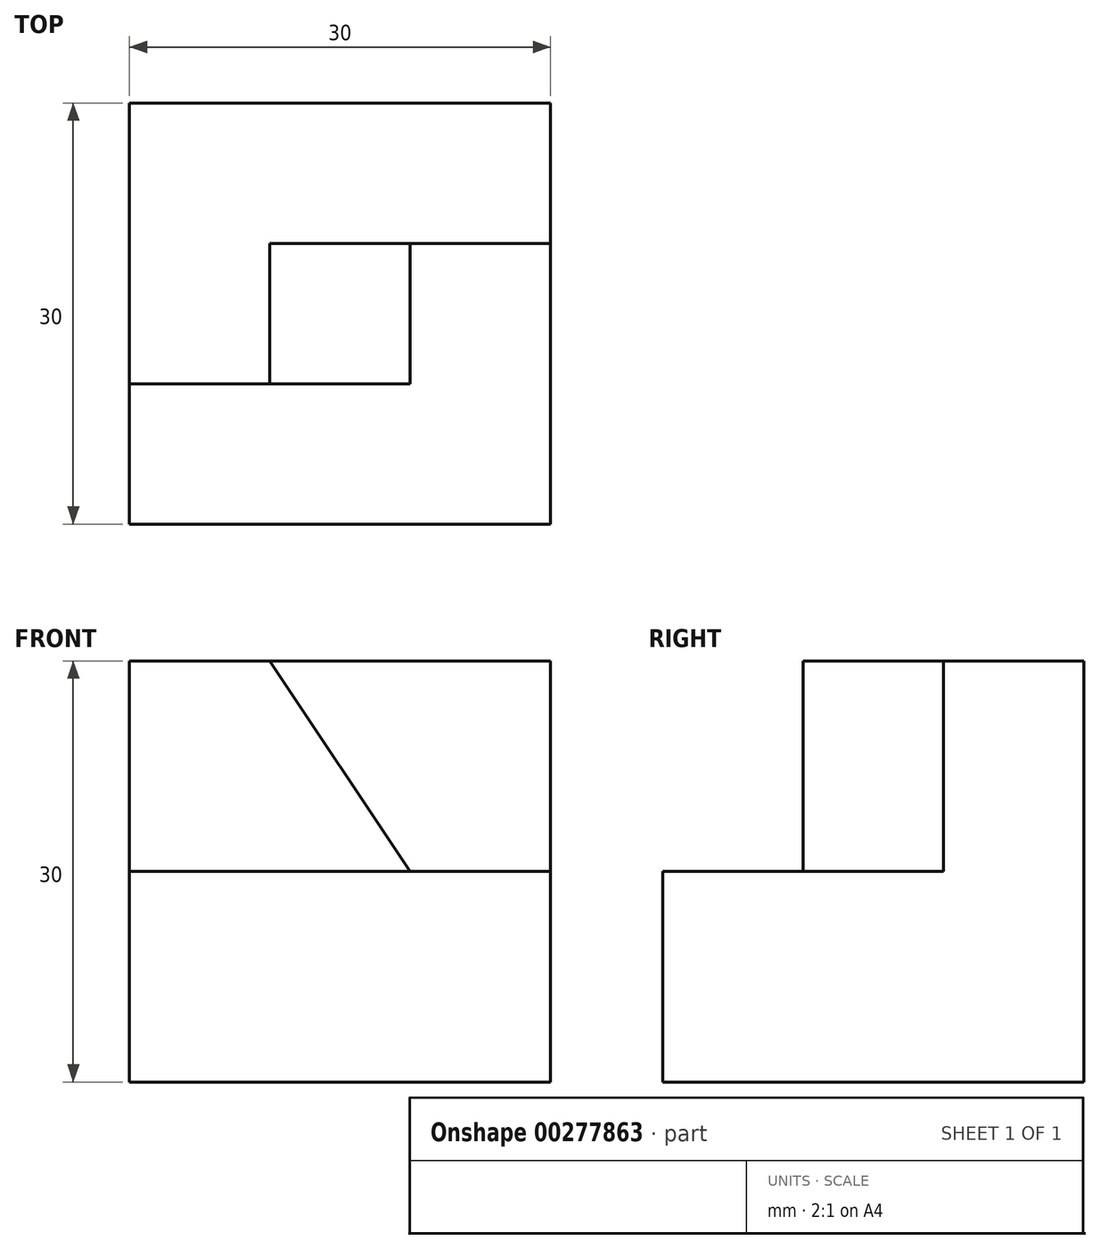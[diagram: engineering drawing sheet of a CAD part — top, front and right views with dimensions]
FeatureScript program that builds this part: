
annotation { "Feature Type Name" : "Feature", "Feature Type Description" : "" }
export const myFeature = defineFeature(function(context is Context, id is Id, definition is map)
    precondition{}
    {
        {
            var Q0;
            Q0=qCreatedBy(makeId("Right.planeOp"),FACE);
            var sketch = newSketch(context, id + "F0", { "sketchPlane" : qUnion([Q0])});
            skLineSegment(sketch, "E0.bottom", {"start": v(0, 0) * mm, "end": v(30, 0) * mm});
            skLineSegment(sketch, "E0.top", {"start": v(0, 30) * mm, "end": v(30, 30) * mm});
            skLineSegment(sketch, "E0.left", {"start": v(0, 0) * mm, "end": v(0, 30) * mm});
            skLineSegment(sketch, "E0.right", {"start": v(30, 0) * mm, "end": v(30, 30) * mm});
            skLineSegment(sketch, "E1", {"start": v(0, 15) * mm, "end": v(10, 15) * mm});
            skLineSegment(sketch, "E2", {"start": v(10, 15) * mm, "end": v(10, 30) * mm});
            skSolve(sketch);
        }
        {
            var Q0;
            {var subQ2=sQuery(id+"F0.wireOp",EDGE,"E0.bottom");Q0=makeQuery(id+"F0.imprint","IMPRINT",FACE,{"disambiguationData":[TD([[makeQuery(id+"F0.imprint","IMPRINT",EDGE,{"derivedFrom":subQ2}),1.0]])]});}
            extrude(context, id + "F1", {"entities" : qUnion([Q0]), "depth" : 30 * mm});
        }
        {
            var Q0;
            Q0=makeQuery(id+"F1.opExtrude","SWEPT_FACE",FACE,{"disambiguationData":[OSD([sQuery(id+"F0.wireOp",EDGE,"E2")])]});
            var sketch = newSketch(context, id + "F2", { "sketchPlane" : qUnion([Q0])});
            skLineSegment(sketch, "E3.0", {"start": v(30, 30) * mm, "end": v(0, 30) * mm});
            skLineSegment(sketch, "E4.0", {"start": v(30, 15) * mm, "end": v(30, 30) * mm});
            skLineSegment(sketch, "E5.0", {"start": v(30, 15) * mm, "end": v(0, 15) * mm});
            skLineSegment(sketch, "E6", {"start": v(10, 30) * mm, "end": v(20, 15) * mm});
            skSolve(sketch);
        }
        {
            var Q0;
            Q0 = qSketchRegion(id + "F2", true);
            extrude(context, id + "F3", {"entities" : qUnion([Q0]), "operationType" : NewBodyOperationType.REMOVE, "oppositeDirection" : true, "depth" : 10 * mm});
        }
    });
